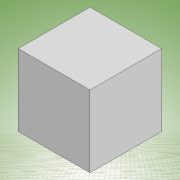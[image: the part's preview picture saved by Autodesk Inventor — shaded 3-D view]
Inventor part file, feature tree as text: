
AUTODESK INVENTOR PART (.ipt)
format: ipt  version: 2022 (Build 260153000, 153)  size: 93,696 bytes
history: native  units: mm
features: other x1, extrude x1, sketch x1
ambient origin geometry x8: Origin, YZ Plane, XZ Plane, XY Plane, X Axis, Y Axis, Z Axis, Center Point
bodies: Body1 (feature_tree)
feature tree (3):
  other  "Sólido1"
  extrude  "Extrusión1"  Depth=50.0mm
  sketch  "Boceto1"  dims[d0=50.0mm d1=50.0mm d2=50.0mm d3=0.0mm]
